# Revit family: 706340001_Válvula para Orinal Flujo Ajustable
name_source: partatom
category: Plumbing Fixtures
units: mm (PartAtom-declared; Revit-internal decimal feet)

## family parameters
Always vertical = Yes
Cut with Voids When Loaded = No
Host = Wall
OmniClass Number = 23.39.27.00
Part Type = Normal
Room Calculation Point = No
Round Connector Dimension = Use Diameter
Shared = No

## types (1)
- Type 1
    Alto = 362 mm  [stored 1.18766 ft]
    Ancho = 280 mm  [stored 0.918635 ft]
    Capacidad de flujo = 4,9 L/min a 50 Psi.
    Ciclo de descarga = 1,9 L/min a 50 Psi
    Consumo de agua = 0.5 lpf a 3.8 lpf.
    Creado por = BIMBAU
    Default Elevation = 0 mm  [stored 0 ft]
    Description = Descarga de agua variable según presión. • Tipo de accionamiento manual de palanca.
• Instalación para lado derecho y/o izquierdo.
• Registro individual que permite el cierre del suministro de agua.
• Incluye rompe vacío para evitar el contra flujo de agua (anti sifón).
    Entrada minimo = 3/4 NPT.
    Fecha de creación = 12/03/2021
    Garantía = 3 años
    Manufacturer = Corona
    Material = Corona_Cromado
    Model = Válvula Orinal de Flujo Ajustable
    Peso Bruto aprox = 2,600g 5,7320lb.
    Peso Neto aprox = 2,270g 5,0045lb.
    Presion maxima = 20 - 80 Psi.
    Presion minima = 20 Psi.
    Profundidad = 135 mm  [stored 0.442913 ft]
    Referencia = 706340001
    Vida útil = 150 Mil Ciclos.

note: [stored X ft] marks values corroborated as IEEE doubles in the binary element streams (Revit-internal decimal feet)

## geometry (parser evidence)
native form markers: Sweep x7
no freeform markers — native parametric forms only
